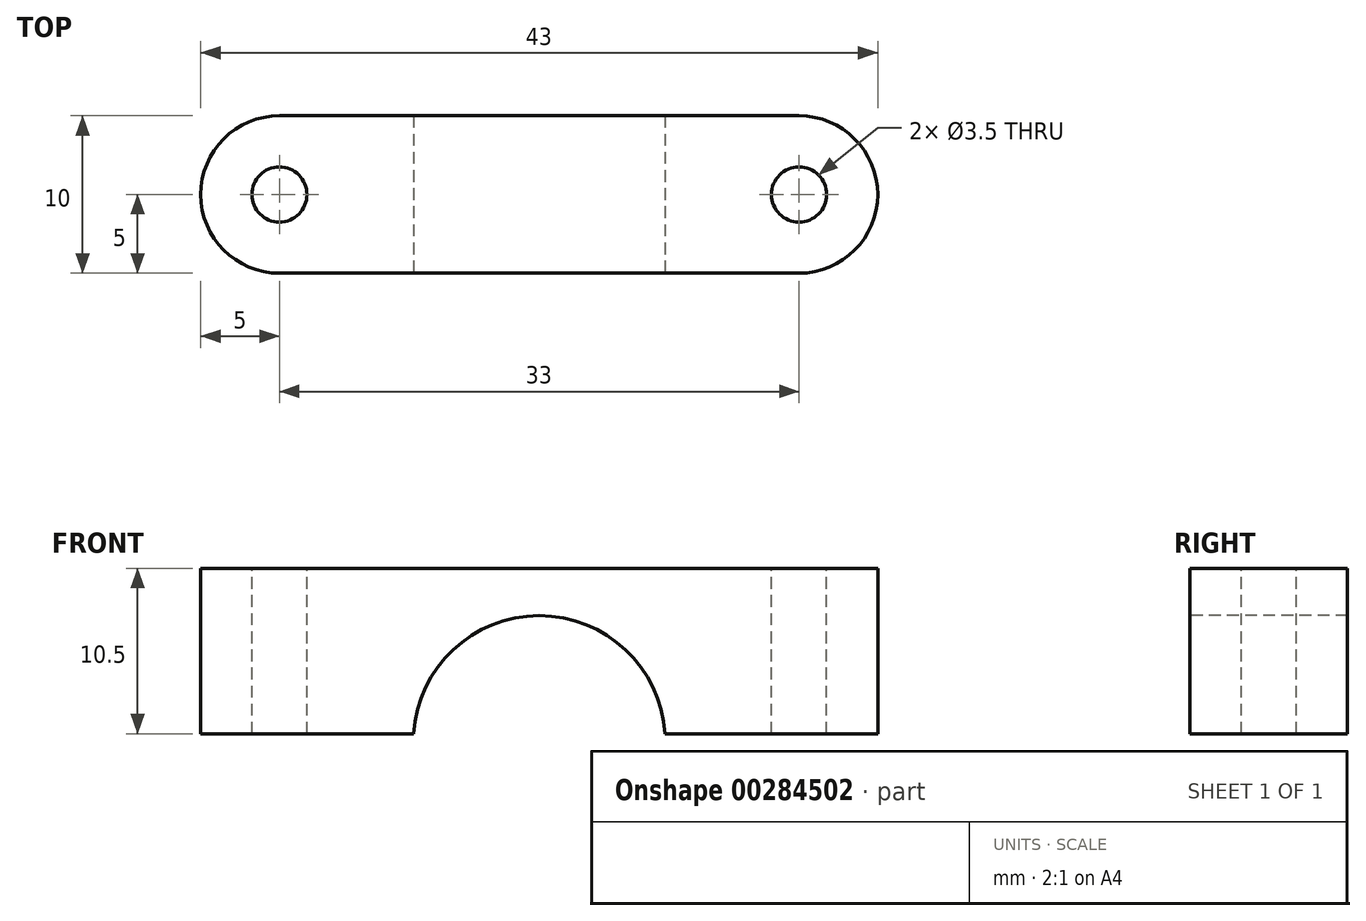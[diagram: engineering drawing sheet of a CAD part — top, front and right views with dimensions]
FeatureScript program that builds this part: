
annotation { "Feature Type Name" : "Feature", "Feature Type Description" : "" }
export const myFeature = defineFeature(function(context is Context, id is Id, definition is map)
    precondition{}
    {
        {
            var Q0;
            Q0=qCreatedBy(makeId("Top.planeOp"),FACE);
            var sketch = newSketch(context, id + "F0", { "sketchPlane" : qUnion([Q0])});
            skArc(sketch, "E0", {"start": v(-16.5, 5) * mm, "mid": v(-21.5, 0) * mm, "end": v(-16.5, -5) * mm});
            skArc(sketch, "E1", {"start": v(16.5, -5) * mm, "mid": v(21.5, 0) * mm, "end": v(16.5, 5) * mm});
            skLineSegment(sketch, "E2", {"start": v(-16.5, -5) * mm, "end": v(16.5, -5) * mm});
            skLineSegment(sketch, "E3", {"start": v(16.5, 5) * mm, "end": v(-16.5, 5) * mm});
            skSolve(sketch);
        }
        {
            var Q0;
            Q0 = qSketchRegion(id + "F0", true);
            extrude(context, id + "F1", {"entities" : qUnion([Q0]), "depth" : 11 * mm});
        }
        {
            var Q0;
            Q0=qCreatedBy(makeId("Front.planeOp"),FACE);
            var sketch = newSketch(context, id + "F2", { "sketchPlane" : qUnion([Q0])});
            skArc(sketch, "E4", {"start": v(8, 0) * mm, "mid": v(0, 8) * mm, "end": v(-8, 0) * mm});
            skLineSegment(sketch, "E5", {"start": v(-8, 0) * mm, "end": v(8, 0) * mm});
            skSolve(sketch);
        }
        {
            var Q0;
            Q0 = qSketchRegion(id + "F2", true);
            extrude(context, id + "F3", {"entities" : qUnion([Q0]), "operationType" : NewBodyOperationType.REMOVE, "endBound" : BoundingType.SYMMETRIC, "oppositeDirection" : true, "depth" : 25 * mm});
        }
        {
            var Q0;
            Q0=makeQuery(id+"F1.opExtrude","CAP_FACE",FACE,{"disambiguationData":[OSD([sQuery(id+"F0.wireOp",EDGE,"E0"),sQuery(id+"F0.wireOp",EDGE,"E1"),sQuery(id+"F0.wireOp",EDGE,"E2"),sQuery(id+"F0.wireOp",EDGE,"E3")])],"isStart":false});
            var sketch = newSketch(context, id + "F4", { "sketchPlane" : qUnion([Q0])});
            skCircle(sketch, "E6", {"center": v(-16.5, 0) * mm, "radius": 1.75 * mm});
            skCircle(sketch, "E7", {"center": v(16.5, 0) * mm, "radius": 1.75 * mm});
            skSolve(sketch);
        }
        {
            var Q0;
            Q0 = qSketchRegion(id + "F4", true);
            extrude(context, id + "F5", {"entities" : qUnion([Q0]), "operationType" : NewBodyOperationType.REMOVE, "oppositeDirection" : true, "depth" : 25 * mm});
        }
        {
            var Q0;
            Q0=qCreatedBy(makeId("Front.planeOp"),FACE);
            var sketch = newSketch(context, id + "F6", { "sketchPlane" : qUnion([Q0])});
            skLineSegment(sketch, "E8.bottom", {"start": v(22.5, -0.5) * mm, "end": v(-22.5, -0.5) * mm});
            skLineSegment(sketch, "E8.top", {"start": v(22.5, 0.5) * mm, "end": v(-22.5, 0.5) * mm});
            skLineSegment(sketch, "E8.left", {"start": v(22.5, -0.5) * mm, "end": v(22.5, 0.5) * mm});
            skLineSegment(sketch, "E8.right", {"start": v(-22.5, -0.5) * mm, "end": v(-22.5, 0.5) * mm});
            skPoint(sketch, "E8.middle", {"position": v(0, 0) * mm});
            skSolve(sketch);
        }
        {
            var Q0;
            Q0 = qSketchRegion(id + "F6", true);
            extrude(context, id + "F7", {"entities" : qUnion([Q0]), "operationType" : NewBodyOperationType.REMOVE, "endBound" : BoundingType.SYMMETRIC, "depth" : 25 * mm});
        }
    });
